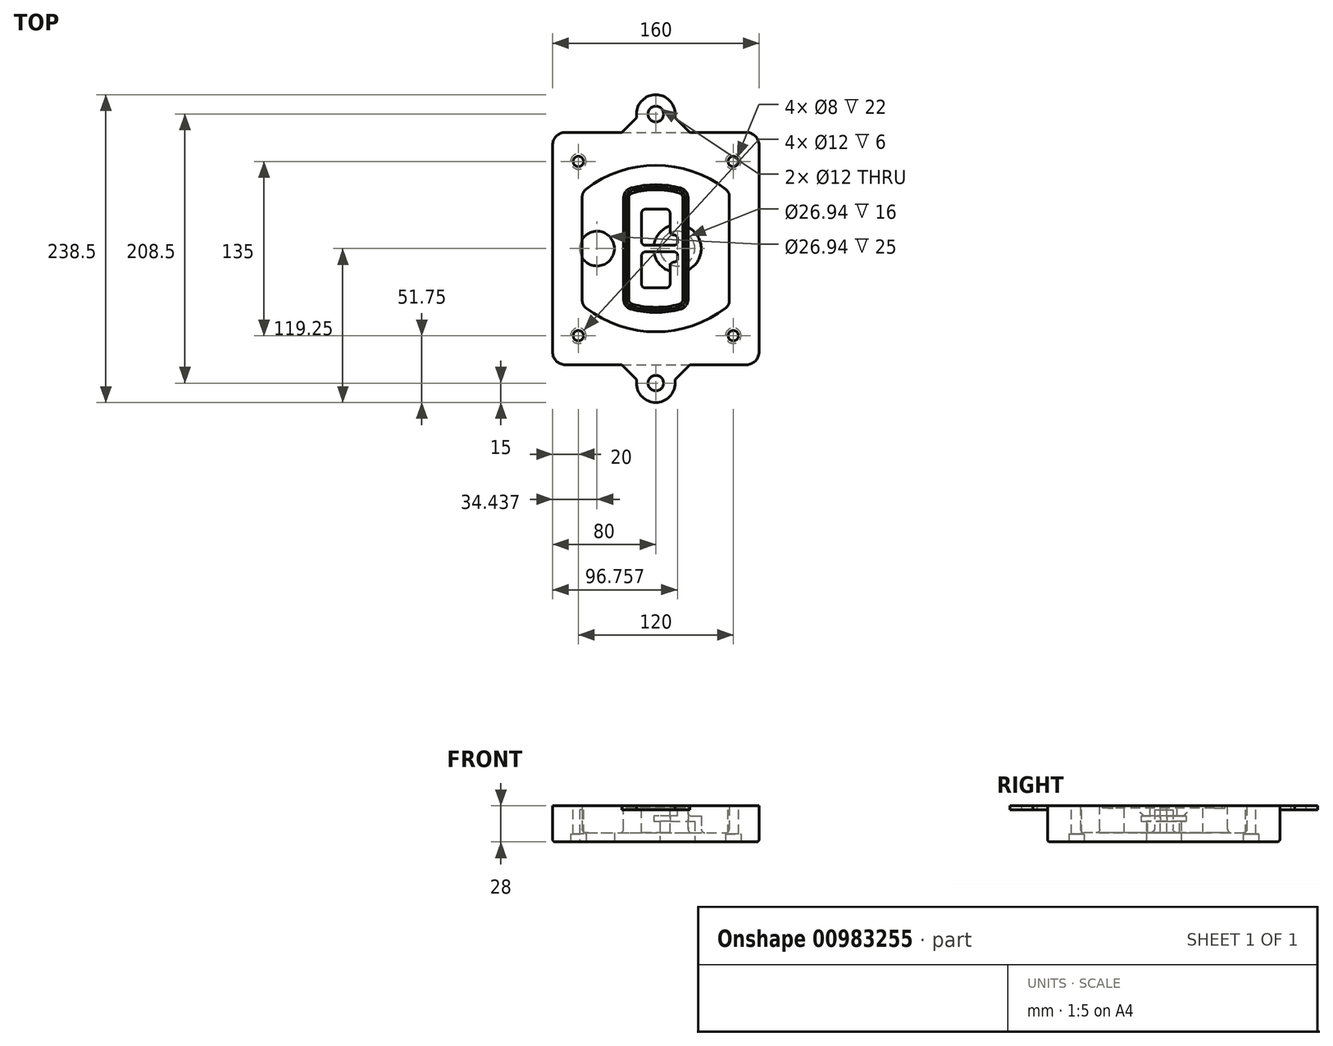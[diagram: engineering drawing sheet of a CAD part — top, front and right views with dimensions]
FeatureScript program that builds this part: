
annotation { "Feature Type Name" : "Feature", "Feature Type Description" : "" }
export const myFeature = defineFeature(function(context is Context, id is Id, definition is map)
    precondition{}
    {
        {
            var Q0;
            Q0=qCreatedBy(makeId("Top.planeOp"),FACE);
            var sketch = newSketch(context, id + "F0", { "sketchPlane" : qUnion([Q0])});
            skPoint(sketch, "E0.rect.middle", {"position": v(0, 0) * mm});
            skLineSegment(sketch, "E1.bottom", {"start": v(-70, -90) * mm, "end": v(70, -90) * mm});
            skLineSegment(sketch, "E1.top", {"start": v(-70, 90) * mm, "end": v(70, 90) * mm});
            skLineSegment(sketch, "E1.left", {"start": v(-80, -80) * mm, "end": v(-80, 80) * mm});
            skLineSegment(sketch, "E1.right", {"start": v(80, -80) * mm, "end": v(80, 80) * mm});
            skLineSegment(sketch, "E2", {"start": v(-80, 90) * mm, "end": v(80, -90) * mm, "construction": true});
            skLineSegment(sketch, "E3", {"start": v(80, 90) * mm, "end": v(-80, -90) * mm, "construction": true});
            skCircle(sketch, "E4", {"center": v(-60, 67.5) * mm, "radius": 4 * mm});
            skCircle(sketch, "E5", {"center": v(60, 67.5) * mm, "radius": 4 * mm});
            skCircle(sketch, "E6", {"center": v(60, -67.5) * mm, "radius": 4 * mm});
            skCircle(sketch, "E7", {"center": v(-60, -67.5) * mm, "radius": 4 * mm});
            skLineSegment(sketch, "E8", {"start": v(-60, 67.5) * mm, "end": v(60, 67.5) * mm, "construction": true});
            skLineSegment(sketch, "E9", {"start": v(60, 67.5) * mm, "end": v(60, -67.5) * mm, "construction": true});
            skLineSegment(sketch, "E10", {"start": v(60, -67.5) * mm, "end": v(-60, -67.5) * mm, "construction": true});
            skLineSegment(sketch, "E11", {"start": v(-60, -67.5) * mm, "end": v(-60, 67.5) * mm, "construction": true});
            skLineSegment(sketch, "E12", {"start": v(-60, 40.3) * mm, "end": v(-60, -40.3) * mm});
            skLineSegment(sketch, "E13", {"start": v(60, 40.3) * mm, "end": v(60, -40.3) * mm});
            skArc(sketch, "E14", {"start": v(56.15, 48.18) * mm, "mid": v(0, 67.5) * mm, "end": v(-56.15, 48.18) * mm});
            skArc(sketch, "E15", {"start": v(-56.15, -48.18) * mm, "mid": v(0, -67.5) * mm, "end": v(56.15, -48.18) * mm});
            skLineSegment(sketch, "E16", {"start": v(-60, 0) * mm, "end": v(60, 0) * mm, "construction": true});
            skPoint(sketch, "E17.visualSharp", {"position": v(-60, -45) * mm});
            skArc(sketch, "E17.filletArc", {"start": v(-60, -40.3) * mm, "mid": v(-58.99, -44.68) * mm, "end": v(-56.15, -48.18) * mm});
            skPoint(sketch, "E18.visualSharp", {"position": v(-60, 45) * mm});
            skArc(sketch, "E18.filletArc", {"start": v(-56.15, 48.18) * mm, "mid": v(-58.99, 44.68) * mm, "end": v(-60, 40.3) * mm});
            skPoint(sketch, "E19.visualSharp", {"position": v(60, 45) * mm});
            skArc(sketch, "E19.filletArc", {"start": v(60, 40.3) * mm, "mid": v(58.99, 44.68) * mm, "end": v(56.15, 48.18) * mm});
            skPoint(sketch, "E20.visualSharp", {"position": v(60, -45) * mm});
            skArc(sketch, "E20.filletArc", {"start": v(56.15, -48.18) * mm, "mid": v(58.99, -44.68) * mm, "end": v(60, -40.3) * mm});
            skPoint(sketch, "E21.visualSharp", {"position": v(-80, 90) * mm});
            skArc(sketch, "E21.filletArc", {"start": v(-70, 90) * mm, "mid": v(-77.07, 87.07) * mm, "end": v(-80, 80) * mm});
            skPoint(sketch, "E22.visualSharp", {"position": v(80, 90) * mm});
            skArc(sketch, "E22.filletArc", {"start": v(80, 80) * mm, "mid": v(77.07, 87.07) * mm, "end": v(70, 90) * mm});
            skPoint(sketch, "E23.visualSharp", {"position": v(80, -90) * mm});
            skArc(sketch, "E23.filletArc", {"start": v(70, -90) * mm, "mid": v(77.07, -87.07) * mm, "end": v(80, -80) * mm});
            skPoint(sketch, "E24.visualSharp", {"position": v(-80, -90) * mm});
            skArc(sketch, "E24.filletArc", {"start": v(-80, -80) * mm, "mid": v(-77.07, -87.07) * mm, "end": v(-70, -90) * mm});
            skArc(sketch, "E25.0", {"start": v(57, 40.3) * mm, "mid": v(56.3, 43.36) * mm, "end": v(54.3, 45.81) * mm});
            skLineSegment(sketch, "E25.1", {"start": v(57, 40.3) * mm, "end": v(57, -40.3) * mm});
            skArc(sketch, "E25.2", {"start": v(54.3, -45.81) * mm, "mid": v(56.3, -43.36) * mm, "end": v(57, -40.3) * mm});
            skArc(sketch, "E25.3", {"start": v(-54.3, -45.81) * mm, "mid": v(0, -64.5) * mm, "end": v(54.3, -45.81) * mm});
            skArc(sketch, "E25.4", {"start": v(-57, -40.3) * mm, "mid": v(-56.3, -43.36) * mm, "end": v(-54.3, -45.81) * mm});
            skArc(sketch, "E25.5", {"start": v(54.3, 45.81) * mm, "mid": v(0, 64.5) * mm, "end": v(-54.3, 45.81) * mm});
            skLineSegment(sketch, "E25.6", {"start": v(-57, 40.3) * mm, "end": v(-57, -40.3) * mm});
            skArc(sketch, "E25.7", {"start": v(-54.3, 45.81) * mm, "mid": v(-56.3, 43.36) * mm, "end": v(-57, 40.3) * mm});
            skArc(sketch, "E26.0", {"start": v(-58.62, 51.33) * mm, "mid": v(-62.58, 46.43) * mm, "end": v(-64, 40.3) * mm});
            skArc(sketch, "E26.1", {"start": v(58.62, 51.33) * mm, "mid": v(0, 71.5) * mm, "end": v(-58.62, 51.33) * mm});
            skArc(sketch, "E26.2", {"start": v(64, 40.3) * mm, "mid": v(62.58, 46.43) * mm, "end": v(58.62, 51.33) * mm});
            skLineSegment(sketch, "E26.3", {"start": v(64, 40.3) * mm, "end": v(64, -40.3) * mm});
            skArc(sketch, "E26.4", {"start": v(58.62, -51.33) * mm, "mid": v(62.58, -46.43) * mm, "end": v(64, -40.3) * mm});
            skLineSegment(sketch, "E26.5", {"start": v(-64, 40.3) * mm, "end": v(-64, -40.3) * mm});
            skArc(sketch, "E26.6", {"start": v(-58.62, -51.33) * mm, "mid": v(0, -71.5) * mm, "end": v(58.62, -51.33) * mm});
            skArc(sketch, "E26.7", {"start": v(-64, -40.3) * mm, "mid": v(-62.58, -46.43) * mm, "end": v(-58.62, -51.33) * mm});
            skSolve(sketch);
        }
        {
            var Q0;
            Q0=makeQuery(id+"F0.imprint","IMPRINT",FACE,{"disambiguationData":[TD([[makeQuery(id+"F0.imprint","IMPRINT",EDGE,{"derivedFrom":sQuery(id+"F0.wireOp",EDGE,"E1.bottom")}),1.0]])]});
            var Q1;
            Q1=makeQuery(id+"F0.imprint","IMPRINT",FACE,{"disambiguationData":[TD([[makeQuery(id+"F0.imprint","IMPRINT",EDGE,{"derivedFrom":sQuery(id+"F0.wireOp",EDGE,"E12")}),1.0]])]});
            var Q2;
            Q2=makeQuery(id+"F0.imprint","IMPRINT",FACE,{"disambiguationData":[TD([[makeQuery(id+"F0.imprint","IMPRINT",EDGE,{"derivedFrom":sQuery(id+"F0.wireOp",EDGE,"E25.0")}),1.0]])]});
            var Q3;
            Q3=makeQuery(id+"F0.imprint","IMPRINT",FACE,{"disambiguationData":[TD([[makeQuery(id+"F0.imprint","IMPRINT",EDGE,{"derivedFrom":sQuery(id+"F0.wireOp",EDGE,"E12")}),-1.0]])]});
            extrude(context, id + "F1", {"entities" : qUnion([Q0, Q1, Q2, Q3]), "oppositeDirection" : true, "depth" : 25 * mm});
        }
        {
            var Q0;
            Q0=makeQuery(id+"F0.imprint","IMPRINT",FACE,{"disambiguationData":[TD([[makeQuery(id+"F0.imprint","IMPRINT",EDGE,{"derivedFrom":sQuery(id+"F0.wireOp",EDGE,"E12")}),1.0]])]});
            extrude(context, id + "F2", {"entities" : qUnion([Q0]), "operationType" : NewBodyOperationType.ADD, "depth" : 3 * mm});
        }
        {
            var Q0;
            Q0=makeQuery(id+"F0.imprint","IMPRINT",FACE,{"disambiguationData":[TD([[makeQuery(id+"F0.imprint","IMPRINT",EDGE,{"derivedFrom":sQuery(id+"F0.wireOp",EDGE,"E25.0")}),1.0]])]});
            extrude(context, id + "F3", {"entities" : qUnion([Q0]), "operationType" : NewBodyOperationType.REMOVE, "oppositeDirection" : true, "depth" : 18 * mm});
        }
        {
            var Q0;
            Q0=makeQuery(id+"F2.opExtrude","CAP_FACE",FACE,{"disambiguationData":[OSD([sQuery(id+"F0.wireOp",EDGE,"E12"),sQuery(id+"F0.wireOp",EDGE,"E13"),sQuery(id+"F0.wireOp",EDGE,"E14"),sQuery(id+"F0.wireOp",EDGE,"E15"),sQuery(id+"F0.wireOp",EDGE,"E17.filletArc"),sQuery(id+"F0.wireOp",EDGE,"E18.filletArc"),sQuery(id+"F0.wireOp",EDGE,"E19.filletArc"),sQuery(id+"F0.wireOp",EDGE,"E20.filletArc"),sQuery(id+"F0.wireOp",EDGE,"E25.0"),sQuery(id+"F0.wireOp",EDGE,"E25.1"),sQuery(id+"F0.wireOp",EDGE,"E25.2"),sQuery(id+"F0.wireOp",EDGE,"E25.3"),sQuery(id+"F0.wireOp",EDGE,"E25.4"),sQuery(id+"F0.wireOp",EDGE,"E25.5"),sQuery(id+"F0.wireOp",EDGE,"E25.6"),sQuery(id+"F0.wireOp",EDGE,"E25.7")])],"isStart":false});
            var sketch = newSketch(context, id + "F4", { "sketchPlane" : qUnion([Q0])});
            skArc(sketch, "E27.0", {"start": v(-19.08, -46.97) * mm, "mid": v(0, -49.5) * mm, "end": v(19.08, -46.97) * mm});
            skArc(sketch, "E28.0", {"start": v(19.08, 46.97) * mm, "mid": v(0, 49.5) * mm, "end": v(-19.08, 46.97) * mm});
            skLineSegment(sketch, "E29", {"start": v(-25, 39.25) * mm, "end": v(-25, -39.25) * mm});
            skLineSegment(sketch, "E30", {"start": v(25, 39.25) * mm, "end": v(25, -39.25) * mm});
            skLineSegment(sketch, "E31", {"start": v(-25, 45.1) * mm, "end": v(25, 45.1) * mm, "construction": true});
            skLineSegment(sketch, "E32", {"start": v(-25, -45.1) * mm, "end": v(25, -45.1) * mm, "construction": true});
            skPoint(sketch, "E33.visualSharp", {"position": v(-25, 45.1) * mm});
            skArc(sketch, "E33.filletArc", {"start": v(-19.08, 46.97) * mm, "mid": v(-23.35, 44.11) * mm, "end": v(-25, 39.25) * mm});
            skPoint(sketch, "E34.visualSharp", {"position": v(25, 45.1) * mm});
            skArc(sketch, "E34.filletArc", {"start": v(25, 39.25) * mm, "mid": v(23.35, 44.11) * mm, "end": v(19.08, 46.97) * mm});
            skPoint(sketch, "E35.visualSharp", {"position": v(25, -45.1) * mm});
            skArc(sketch, "E35.filletArc", {"start": v(19.08, -46.97) * mm, "mid": v(23.35, -44.11) * mm, "end": v(25, -39.25) * mm});
            skPoint(sketch, "E36.visualSharp", {"position": v(-25, -45.1) * mm});
            skArc(sketch, "E36.filletArc", {"start": v(-25, -39.25) * mm, "mid": v(-23.35, -44.11) * mm, "end": v(-19.08, -46.97) * mm});
            skArc(sketch, "E37.0", {"start": v(54.3, 45.81) * mm, "mid": v(0, 64.5) * mm, "end": v(-54.3, 45.81) * mm});
            skArc(sketch, "E37.1", {"start": v(-54.3, 45.81) * mm, "mid": v(-56.3, 43.36) * mm, "end": v(-57, 40.3) * mm});
            skLineSegment(sketch, "E37.2", {"start": v(-57, 40.3) * mm, "end": v(-57, -40.3) * mm});
            skArc(sketch, "E37.3", {"start": v(-57, -40.3) * mm, "mid": v(-56.3, -43.36) * mm, "end": v(-54.3, -45.81) * mm});
            skArc(sketch, "E37.4", {"start": v(-54.3, -45.81) * mm, "mid": v(0, -64.5) * mm, "end": v(54.3, -45.81) * mm});
            skArc(sketch, "E37.5", {"start": v(54.3, -45.81) * mm, "mid": v(56.3, -43.36) * mm, "end": v(57, -40.3) * mm});
            skLineSegment(sketch, "E37.6", {"start": v(57, 40.3) * mm, "end": v(57, -40.3) * mm});
            skArc(sketch, "E37.7", {"start": v(57, 40.3) * mm, "mid": v(56.3, 43.36) * mm, "end": v(54.3, 45.81) * mm});
            skLineSegment(sketch, "E38.0", {"start": v(23, 39.25) * mm, "end": v(23, -39.25) * mm});
            skArc(sketch, "E38.1", {"start": v(18.56, -45.04) * mm, "mid": v(21.76, -42.9) * mm, "end": v(23, -39.25) * mm});
            skArc(sketch, "E38.2", {"start": v(-18.56, -45.04) * mm, "mid": v(0, -47.5) * mm, "end": v(18.56, -45.04) * mm});
            skArc(sketch, "E38.3", {"start": v(-23, -39.25) * mm, "mid": v(-21.76, -42.9) * mm, "end": v(-18.56, -45.04) * mm});
            skLineSegment(sketch, "E38.4", {"start": v(-23, 39.25) * mm, "end": v(-23, -39.25) * mm});
            skArc(sketch, "E38.5", {"start": v(23, 39.25) * mm, "mid": v(21.76, 42.9) * mm, "end": v(18.56, 45.04) * mm});
            skArc(sketch, "E38.6", {"start": v(-18.56, 45.04) * mm, "mid": v(-21.76, 42.9) * mm, "end": v(-23, 39.25) * mm});
            skArc(sketch, "E38.7", {"start": v(18.56, 45.04) * mm, "mid": v(0, 47.5) * mm, "end": v(-18.56, 45.04) * mm});
            skArc(sketch, "E39.0", {"start": v(21, 39.25) * mm, "mid": v(20.18, 41.68) * mm, "end": v(18.04, 43.1) * mm});
            skLineSegment(sketch, "E39.1", {"start": v(21, 39.25) * mm, "end": v(21, -39.25) * mm});
            skArc(sketch, "E39.2", {"start": v(18.04, -43.1) * mm, "mid": v(20.18, -41.68) * mm, "end": v(21, -39.25) * mm});
            skArc(sketch, "E39.3", {"start": v(-18.04, -43.1) * mm, "mid": v(0, -45.5) * mm, "end": v(18.04, -43.1) * mm});
            skArc(sketch, "E39.4", {"start": v(-21, -39.25) * mm, "mid": v(-20.18, -41.68) * mm, "end": v(-18.04, -43.1) * mm});
            skArc(sketch, "E39.5", {"start": v(18.04, 43.1) * mm, "mid": v(0, 45.5) * mm, "end": v(-18.04, 43.1) * mm});
            skLineSegment(sketch, "E39.6", {"start": v(-21, 39.25) * mm, "end": v(-21, -39.25) * mm});
            skArc(sketch, "E39.7", {"start": v(-18.04, 43.1) * mm, "mid": v(-20.18, 41.68) * mm, "end": v(-21, 39.25) * mm});
            skLineSegment(sketch, "E40", {"start": v(-25, 0) * mm, "end": v(25, 0) * mm, "construction": true});
            skLineSegment(sketch, "E41", {"start": v(-11, 5.5) * mm, "end": v(-11, 27.5) * mm});
            skLineSegment(sketch, "E42", {"start": v(-8, 30.5) * mm, "end": v(8, 30.5) * mm});
            skLineSegment(sketch, "E43", {"start": v(11, 27.5) * mm, "end": v(11, 13.5) * mm});
            skLineSegment(sketch, "E44", {"start": v(14, 10.5) * mm, "end": v(14, 10.5) * mm});
            skLineSegment(sketch, "E45", {"start": v(17, 7.5) * mm, "end": v(17, 5.5) * mm});
            skLineSegment(sketch, "E46", {"start": v(14, 2.5) * mm, "end": v(-8, 2.5) * mm});
            skPoint(sketch, "E47.visualSharp", {"position": v(-11, 30.5) * mm});
            skArc(sketch, "E47.filletArc", {"start": v(-8, 30.5) * mm, "mid": v(-10.12, 29.62) * mm, "end": v(-11, 27.5) * mm});
            skPoint(sketch, "E48.visualSharp", {"position": v(11, 30.5) * mm});
            skArc(sketch, "E48.filletArc", {"start": v(11, 27.5) * mm, "mid": v(10.12, 29.62) * mm, "end": v(8, 30.5) * mm});
            skPoint(sketch, "E49.visualSharp", {"position": v(11, 10.5) * mm});
            skArc(sketch, "E49.filletArc", {"start": v(11, 13.5) * mm, "mid": v(11.88, 11.38) * mm, "end": v(14, 10.5) * mm});
            skPoint(sketch, "E50.visualSharp", {"position": v(17, 10.5) * mm});
            skArc(sketch, "E50.filletArc", {"start": v(17, 7.5) * mm, "mid": v(16.12, 9.62) * mm, "end": v(14, 10.5) * mm});
            skPoint(sketch, "E51.visualSharp", {"position": v(17, 2.5) * mm});
            skArc(sketch, "E51.filletArc", {"start": v(14, 2.5) * mm, "mid": v(16.12, 3.38) * mm, "end": v(17, 5.5) * mm});
            skPoint(sketch, "E52.visualSharp", {"position": v(-11, 2.5) * mm});
            skArc(sketch, "E52.filletArc", {"start": v(-11, 5.5) * mm, "mid": v(-10.12, 3.38) * mm, "end": v(-8, 2.5) * mm});
            skLineSegment(sketch, "E53.0.MirrorCS", {"start": v(14, -2.5) * mm, "end": v(-8, -2.5) * mm});
            skArc(sketch, "E54.0.MirrorCS", {"start": v(-11, -5.5) * mm, "mid": v(-10.12, -3.38) * mm, "end": v(-8, -2.5) * mm});
            skLineSegment(sketch, "E55.0.MirrorCS", {"start": v(-11, -5.5) * mm, "end": v(-11, -27.5) * mm});
            skArc(sketch, "E56.0.MirrorCS", {"start": v(-8, -30.5) * mm, "mid": v(-10.12, -29.62) * mm, "end": v(-11, -27.5) * mm});
            skLineSegment(sketch, "E57.0.MirrorCS", {"start": v(-8, -30.5) * mm, "end": v(8, -30.5) * mm});
            skArc(sketch, "E58.0.MirrorCS", {"start": v(11, -27.5) * mm, "mid": v(10.12, -29.62) * mm, "end": v(8, -30.5) * mm});
            skLineSegment(sketch, "E59.0.MirrorCS", {"start": v(11, -27.5) * mm, "end": v(11, -13.5) * mm});
            skArc(sketch, "E60.0.MirrorCS", {"start": v(11, -13.5) * mm, "mid": v(11.88, -11.38) * mm, "end": v(14, -10.5) * mm});
            skArc(sketch, "E61.0.MirrorCS", {"start": v(17, -7.5) * mm, "mid": v(16.12, -9.62) * mm, "end": v(14, -10.5) * mm});
            skLineSegment(sketch, "E62.0.MirrorCS", {"start": v(17, -7.5) * mm, "end": v(17, -5.5) * mm});
            skArc(sketch, "E63.0.MirrorCS", {"start": v(14, -2.5) * mm, "mid": v(16.12, -3.38) * mm, "end": v(17, -5.5) * mm});
            skSolve(sketch);
        }
        {
            var Q0;
            Q0=makeQuery(id+"F4.imprint","IMPRINT",FACE,{"disambiguationData":[TD([[makeQuery(id+"F4.imprint","IMPRINT",EDGE,{"derivedFrom":sQuery(id+"F4.wireOp",EDGE,"E27.0")}),1.0]])]});
            var Q1;
            Q1=makeQuery(id+"F4.imprint","IMPRINT",FACE,{"disambiguationData":[TD([[makeQuery(id+"F4.imprint","IMPRINT",EDGE,{"derivedFrom":sQuery(id+"F4.wireOp",EDGE,"E38.0")}),-1.0]])]});
            var Q2;
            Q2=makeQuery(id+"F4.imprint","IMPRINT",FACE,{"disambiguationData":[TD([[makeQuery(id+"F4.imprint","IMPRINT",EDGE,{"derivedFrom":sQuery(id+"F4.wireOp",EDGE,"E39.0")}),1.0]])]});
            extrude(context, id + "F5", {"entities" : qUnion([Q0, Q1, Q2]), "operationType" : NewBodyOperationType.ADD, "endBound" : BoundingType.UP_TO_NEXT, "oppositeDirection" : true, "depth" : 25 * mm});
        }
        {
            var Q0;
            Q0=makeQuery(id+"F4.imprint","IMPRINT",FACE,{"disambiguationData":[TD([[makeQuery(id+"F4.imprint","IMPRINT",EDGE,{"derivedFrom":sQuery(id+"F4.wireOp",EDGE,"E38.0")}),-1.0]])]});
            extrude(context, id + "F6", {"entities" : qUnion([Q0]), "operationType" : NewBodyOperationType.REMOVE, "oppositeDirection" : true, "depth" : 2 * mm});
        }
        {
            var Q0;
            Q0=makeQuery(id+"F1.opExtrude","CAP_FACE",FACE,{"disambiguationData":[OSD([sQuery(id+"F0.wireOp",EDGE,"E1.bottom"),sQuery(id+"F0.wireOp",EDGE,"E1.top"),sQuery(id+"F0.wireOp",EDGE,"E1.left"),sQuery(id+"F0.wireOp",EDGE,"E1.right"),sQuery(id+"F0.wireOp",EDGE,"E4"),sQuery(id+"F0.wireOp",EDGE,"E5"),sQuery(id+"F0.wireOp",EDGE,"E6"),sQuery(id+"F0.wireOp",EDGE,"E7"),sQuery(id+"F0.wireOp",EDGE,"E21.filletArc"),sQuery(id+"F0.wireOp",EDGE,"E22.filletArc"),sQuery(id+"F0.wireOp",EDGE,"E23.filletArc"),sQuery(id+"F0.wireOp",EDGE,"E24.filletArc")])],"isStart":false});
            var sketch = newSketch(context, id + "F7", { "sketchPlane" : qUnion([Q0])});
            skCircle(sketch, "E64", {"center": v(16.76, 0) * mm, "radius": 13.47 * mm});
            skCircle(sketch, "E65", {"center": v(-45.56, 0) * mm, "radius": 13.47 * mm});
            skLineSegment(sketch, "E66", {"start": v(80, 0) * mm, "end": v(-80, 0) * mm});
            skCircle(sketch, "E67", {"center": v(16.76, 0) * mm, "radius": 18.47 * mm});
            skCircle(sketch, "E68", {"center": v(60, -67.5) * mm, "radius": 6 * mm});
            skCircle(sketch, "E69", {"center": v(-60, -67.5) * mm, "radius": 6 * mm});
            skCircle(sketch, "E70", {"center": v(-60, 67.5) * mm, "radius": 6 * mm});
            skCircle(sketch, "E71", {"center": v(60, 67.5) * mm, "radius": 6 * mm});
            skSolve(sketch);
        }
        {
            var Q0;
            {var subQ1=sQuery(id+"F7.wireOp",EDGE,"E66");var subQ4=sQuery(id+"F7.wireOp",EDGE,"E64");var subQ6=makeQuery(id+"F7.imprint","INTERSECT",VERTEX,{"disambiguationData":[OD(0.0)],"derivedFrom":[subQ4,subQ1]});Q0=makeQuery(id+"F7.imprint","IMPRINT",FACE,{"disambiguationData":[TD([[makeQuery(id+"F7.imprint","IMPRINT",EDGE,{"disambiguationData":[TD([[subQ6,-1.0]])],"derivedFrom":subQ4}),-1.0]])]});}
            var Q1;
            {var subQ0=sQuery(id+"F7.wireOp",EDGE,"E66");var subQ1=sQuery(id+"F7.wireOp",EDGE,"E64");var subQ3=makeQuery(id+"F7.imprint","INTERSECT",VERTEX,{"disambiguationData":[OD(0.0)],"derivedFrom":[subQ1,subQ0]});Q1=makeQuery(id+"F7.imprint","IMPRINT",FACE,{"disambiguationData":[TD([[makeQuery(id+"F7.imprint","IMPRINT",EDGE,{"disambiguationData":[TD([[subQ3,-1.0]])],"derivedFrom":subQ1}),1.0]])]});}
            var Q2;
            {var subQ0=sQuery(id+"F7.wireOp",EDGE,"E66");var subQ1=sQuery(id+"F7.wireOp",EDGE,"E64");var subQ3=makeQuery(id+"F7.imprint","INTERSECT",VERTEX,{"disambiguationData":[OD(0.0)],"derivedFrom":[subQ1,subQ0]});Q2=makeQuery(id+"F7.imprint","IMPRINT",FACE,{"disambiguationData":[TD([[makeQuery(id+"F7.imprint","IMPRINT",EDGE,{"disambiguationData":[TD([[subQ3,1.0]])],"derivedFrom":subQ1}),1.0]])]});}
            var Q3;
            {var subQ1=sQuery(id+"F7.wireOp",EDGE,"E66");var subQ4=sQuery(id+"F7.wireOp",EDGE,"E64");var subQ6=makeQuery(id+"F7.imprint","INTERSECT",VERTEX,{"disambiguationData":[OD(0.0)],"derivedFrom":[subQ4,subQ1]});Q3=makeQuery(id+"F7.imprint","IMPRINT",FACE,{"disambiguationData":[TD([[makeQuery(id+"F7.imprint","IMPRINT",EDGE,{"disambiguationData":[TD([[subQ6,1.0]])],"derivedFrom":subQ4}),-1.0]])]});}
            extrude(context, id + "F8", {"entities" : qUnion([Q0, Q1, Q2, Q3]), "operationType" : NewBodyOperationType.ADD, "oppositeDirection" : true, "depth" : 20 * mm});
        }
        {
            var Q0;
            {var subQ0=sQuery(id+"F7.wireOp",EDGE,"E66");var subQ1=sQuery(id+"F7.wireOp",EDGE,"E64");var subQ3=makeQuery(id+"F7.imprint","INTERSECT",VERTEX,{"disambiguationData":[OD(0.0)],"derivedFrom":[subQ1,subQ0]});Q0=makeQuery(id+"F7.imprint","IMPRINT",FACE,{"disambiguationData":[TD([[makeQuery(id+"F7.imprint","IMPRINT",EDGE,{"disambiguationData":[TD([[subQ3,-1.0]])],"derivedFrom":subQ1}),1.0]])]});}
            var Q1;
            {var subQ0=sQuery(id+"F7.wireOp",EDGE,"E66");var subQ1=sQuery(id+"F7.wireOp",EDGE,"E64");var subQ3=makeQuery(id+"F7.imprint","INTERSECT",VERTEX,{"disambiguationData":[OD(0.0)],"derivedFrom":[subQ1,subQ0]});Q1=makeQuery(id+"F7.imprint","IMPRINT",FACE,{"disambiguationData":[TD([[makeQuery(id+"F7.imprint","IMPRINT",EDGE,{"disambiguationData":[TD([[subQ3,1.0]])],"derivedFrom":subQ1}),1.0]])]});}
            extrude(context, id + "F9", {"entities" : qUnion([Q0, Q1]), "operationType" : NewBodyOperationType.REMOVE, "oppositeDirection" : true, "depth" : 16 * mm});
        }
        {
            var Q0;
            {var subQ0=sQuery(id+"F7.wireOp",EDGE,"E66");var subQ1=sQuery(id+"F7.wireOp",EDGE,"E65");var subQ3=makeQuery(id+"F7.imprint","INTERSECT",VERTEX,{"disambiguationData":[OD(0.0)],"derivedFrom":[subQ1,subQ0]});Q0=makeQuery(id+"F7.imprint","IMPRINT",FACE,{"disambiguationData":[TD([[makeQuery(id+"F7.imprint","IMPRINT",EDGE,{"disambiguationData":[TD([[subQ3,-1.0]])],"derivedFrom":subQ1}),1.0]])]});}
            var Q1;
            {var subQ0=sQuery(id+"F7.wireOp",EDGE,"E66");var subQ1=sQuery(id+"F7.wireOp",EDGE,"E65");var subQ3=makeQuery(id+"F7.imprint","INTERSECT",VERTEX,{"disambiguationData":[OD(0.0)],"derivedFrom":[subQ1,subQ0]});Q1=makeQuery(id+"F7.imprint","IMPRINT",FACE,{"disambiguationData":[TD([[makeQuery(id+"F7.imprint","IMPRINT",EDGE,{"disambiguationData":[TD([[subQ3,1.0]])],"derivedFrom":subQ1}),1.0]])]});}
            extrude(context, id + "F10", {"entities" : qUnion([Q0, Q1]), "operationType" : NewBodyOperationType.REMOVE, "oppositeDirection" : true, "depth" : 25 * mm});
        }
        {
            var Q0;
            Q0=makeQuery(id+"F7.imprint","IMPRINT",FACE,{"disambiguationData":[TD([[makeQuery(id+"F7.imprint","IMPRINT",EDGE,{"derivedFrom":sQuery(id+"F7.wireOp",EDGE,"E68")}),1.0]])]});
            var Q1;
            Q1=makeQuery(id+"F7.imprint","IMPRINT",FACE,{"disambiguationData":[TD([[makeQuery(id+"F7.imprint","IMPRINT",EDGE,{"derivedFrom":makeQuery(id+"F1.opExtrude","CAP_EDGE",EDGE,{"disambiguationData":[OSD([sQuery(id+"F0.wireOp",EDGE,"E5")])],"isStart":false})}),-1.0]])]});
            var Q2;
            Q2=makeQuery(id+"F7.imprint","IMPRINT",FACE,{"disambiguationData":[TD([[makeQuery(id+"F7.imprint","IMPRINT",EDGE,{"derivedFrom":sQuery(id+"F7.wireOp",EDGE,"E69")}),1.0]])]});
            var Q3;
            Q3=makeQuery(id+"F7.imprint","IMPRINT",FACE,{"disambiguationData":[TD([[makeQuery(id+"F7.imprint","IMPRINT",EDGE,{"derivedFrom":makeQuery(id+"F1.opExtrude","CAP_EDGE",EDGE,{"disambiguationData":[OSD([sQuery(id+"F0.wireOp",EDGE,"E4")])],"isStart":false})}),-1.0]])]});
            var Q4;
            Q4=makeQuery(id+"F7.imprint","IMPRINT",FACE,{"disambiguationData":[TD([[makeQuery(id+"F7.imprint","IMPRINT",EDGE,{"derivedFrom":sQuery(id+"F7.wireOp",EDGE,"E70")}),1.0]])]});
            var Q5;
            Q5=makeQuery(id+"F7.imprint","IMPRINT",FACE,{"disambiguationData":[TD([[makeQuery(id+"F7.imprint","IMPRINT",EDGE,{"derivedFrom":makeQuery(id+"F1.opExtrude","CAP_EDGE",EDGE,{"disambiguationData":[OSD([sQuery(id+"F0.wireOp",EDGE,"E7")])],"isStart":false})}),-1.0]])]});
            var Q6;
            Q6=makeQuery(id+"F7.imprint","IMPRINT",FACE,{"disambiguationData":[TD([[makeQuery(id+"F7.imprint","IMPRINT",EDGE,{"derivedFrom":sQuery(id+"F7.wireOp",EDGE,"E71")}),1.0]])]});
            var Q7;
            Q7=makeQuery(id+"F7.imprint","IMPRINT",FACE,{"disambiguationData":[TD([[makeQuery(id+"F7.imprint","IMPRINT",EDGE,{"derivedFrom":makeQuery(id+"F1.opExtrude","CAP_EDGE",EDGE,{"disambiguationData":[OSD([sQuery(id+"F0.wireOp",EDGE,"E6")])],"isStart":false})}),-1.0]])]});
            extrude(context, id + "F11", {"entities" : qUnion([Q0, Q1, Q2, Q3, Q4, Q5, Q6, Q7]), "operationType" : NewBodyOperationType.REMOVE, "oppositeDirection" : true, "depth" : 6 * mm});
        }
        {
            var Q0;
            Q0=makeQuery(id+"F9.boolean.opBoolean","COPY",FACE,{"derivedFrom":makeQuery(id+"F9.opExtrude","CAP_FACE",FACE,{"disambiguationData":[OSD([sQuery(id+"F7.wireOp",EDGE,"E64")])],"isStart":false})});
            var sketch = newSketch(context, id + "F12", { "sketchPlane" : qUnion([Q0])});
            skArc(sketch, "E72.0", {"start": v(11, 17.55) * mm, "mid": v(2.57, 11.82) * mm, "end": v(-1.54, 2.5) * mm});
            skArc(sketch, "E72.1", {"start": v(-1.54, -2.5) * mm, "mid": v(2.57, -11.82) * mm, "end": v(11, -17.55) * mm});
            skLineSegment(sketch, "E73", {"start": v(-1.54, -2.5) * mm, "end": v(14, -2.5) * mm});
            skLineSegment(sketch, "E74.0", {"start": v(14, 2.5) * mm, "end": v(-1.54, 2.5) * mm});
            skArc(sketch, "E74.1", {"start": v(14, 2.5) * mm, "mid": v(16.12, 3.38) * mm, "end": v(17, 5.5) * mm});
            skLineSegment(sketch, "E74.2", {"start": v(17, 7.5) * mm, "end": v(17, 5.5) * mm});
            skArc(sketch, "E74.3", {"start": v(17, 7.5) * mm, "mid": v(16.12, 9.62) * mm, "end": v(14, 10.5) * mm});
            skArc(sketch, "E74.4", {"start": v(11, 13.5) * mm, "mid": v(11.88, 11.38) * mm, "end": v(14, 10.5) * mm});
            skLineSegment(sketch, "E74.5", {"start": v(11, 17.55) * mm, "end": v(11, 13.5) * mm});
            skLineSegment(sketch, "E74.7", {"start": v(14, -2.5) * mm, "end": v(-1.54, -2.5) * mm});
            skArc(sketch, "E74.8", {"start": v(14, -2.5) * mm, "mid": v(16.12, -3.38) * mm, "end": v(17, -5.5) * mm});
            skLineSegment(sketch, "E74.9", {"start": v(17, -7.5) * mm, "end": v(17, -5.5) * mm});
            skArc(sketch, "E74.10", {"start": v(17, -7.5) * mm, "mid": v(16.12, -9.62) * mm, "end": v(14, -10.5) * mm});
            skArc(sketch, "E74.11", {"start": v(11, -13.5) * mm, "mid": v(11.88, -11.38) * mm, "end": v(14, -10.5) * mm});
            skLineSegment(sketch, "E74.12", {"start": v(11, -17.55) * mm, "end": v(11, -13.5) * mm});
            skPoint(sketch, "E75.orphan", {"position": v(11, -27.5) * mm});
            skPoint(sketch, "E76.orphan", {"position": v(-8, -2.5) * mm});
            skPoint(sketch, "E77.orphan", {"position": v(-8, 2.5) * mm});
            skPoint(sketch, "E78.orphan", {"position": v(11, 27.5) * mm});
            skSolve(sketch);
        }
        {
            var Q0;
            {var subQ7=sQuery(id+"F12.wireOp",EDGE,"E72.0");var subQ14=sQuery(id+"F12.wireOp",EDGE,"E72.1");var subQ16=sQuery(id+"F12.wireOp",EDGE,"E74.1");var subQ18=sQuery(id+"F12.wireOp",EDGE,"E74.8");Q0=qUnion([makeQuery(id+"F12.imprint","IMPRINT",FACE,{"disambiguationData":[TD([[makeQuery(id+"F12.imprint","IMPRINT",EDGE,{"derivedFrom":subQ7}),1.0]])]}),makeQuery(id+"F12.imprint","IMPRINT",FACE,{"disambiguationData":[TD([[makeQuery(id+"F12.imprint","IMPRINT",EDGE,{"derivedFrom":subQ14}),1.0]])]}),makeQuery(id+"F12.imprint","IMPRINT",FACE,{"disambiguationData":[TD([[makeQuery(id+"F12.imprint","IMPRINT",EDGE,{"derivedFrom":subQ16}),1.0]])]}),makeQuery(id+"F12.imprint","IMPRINT",FACE,{"disambiguationData":[TD([[makeQuery(id+"F12.imprint","IMPRINT",EDGE,{"derivedFrom":subQ18}),-1.0]])]})]);}
            var Q1;
            Q1=makeQuery(id+"F5.boolean.opBoolean","SPLIT",FACE,{"disambiguationData":[TD([makeQuery(id+"F5.opExtrude","SWEPT_FACE",FACE,{"disambiguationData":[OSD([sQuery(id+"F4.wireOp",EDGE,"E41")])]})])],"derivedFrom":makeQuery(id+"F3.boolean.opBoolean","COPY",FACE,{"derivedFrom":makeQuery(id+"F3.opExtrude","CAP_FACE",FACE,{"disambiguationData":[OSD([sQuery(id+"F0.wireOp",EDGE,"E25.0"),sQuery(id+"F0.wireOp",EDGE,"E25.1"),sQuery(id+"F0.wireOp",EDGE,"E25.2"),sQuery(id+"F0.wireOp",EDGE,"E25.3"),sQuery(id+"F0.wireOp",EDGE,"E25.4"),sQuery(id+"F0.wireOp",EDGE,"E25.5"),sQuery(id+"F0.wireOp",EDGE,"E25.6"),sQuery(id+"F0.wireOp",EDGE,"E25.7")])],"isStart":false})})});
            extrude(context, id + "F13", {"entities" : qUnion([Q0]), "operationType" : NewBodyOperationType.REMOVE, "endBound" : BoundingType.UP_TO_SURFACE, "endBoundEntityFace" : qUnion([Q1]), "depth" : 25 * mm});
        }
        {
            var Q0;
            Q0=makeQuery(id+"F3.boolean.opBoolean","COPY",EDGE,{"derivedFrom":makeQuery(id+"F3.opExtrude","CAP_EDGE",EDGE,{"disambiguationData":[OSD([sQuery(id+"F0.wireOp",EDGE,"E25.6")])],"isStart":false})});
            var Q1;
            Q1=makeQuery(id+"F8.boolean.opBoolean","INTERSECT",EDGE,{"derivedFrom":[makeQuery(id+"F5.opExtrude","SWEPT_FACE",FACE,{"disambiguationData":[OSD([sQuery(id+"F4.wireOp",EDGE,"E30")])]}),makeQuery(id+"F8.opExtrude","CAP_FACE",FACE,{"disambiguationData":[OSD([sQuery(id+"F7.wireOp",EDGE,"E67")])],"isStart":false})]});
            var Q2;
            Q2=makeQuery(id+"F8.boolean.opBoolean","INTERSECT",EDGE,{"disambiguationData":[OD(1.0)],"derivedFrom":[makeQuery(id+"F5.opExtrude","SWEPT_FACE",FACE,{"disambiguationData":[OSD([sQuery(id+"F4.wireOp",EDGE,"E30")])]}),makeQuery(id+"F8.opExtrude","SWEPT_FACE",FACE,{"disambiguationData":[OSD([sQuery(id+"F7.wireOp",EDGE,"E67")])]})]});
            var Q3;
            {var subQ0=sQuery(id+"F4.wireOp",EDGE,"E30");Q3=makeQuery(id+"F8.boolean.opBoolean","SPLIT",EDGE,{"disambiguationData":[TD([makeQuery(id+"F5.opExtrude","SWEPT_FACE",FACE,{"disambiguationData":[OSD([sQuery(id+"F4.wireOp",EDGE,"E35.filletArc")])]})])],"derivedFrom":makeQuery(id+"F5.opExtrude","CAP_EDGE",EDGE,{"disambiguationData":[OSD([subQ0])],"isStart":false})});}
            var Q4;
            {var subQ0=sQuery(id+"F0.wireOp",EDGE,"E25.7");var subQ1=sQuery(id+"F0.wireOp",EDGE,"E25.1");var subQ2=sQuery(id+"F0.wireOp",EDGE,"E25.6");var subQ3=sQuery(id+"F0.wireOp",EDGE,"E25.5");var subQ4=sQuery(id+"F0.wireOp",EDGE,"E25.4");var subQ5=sQuery(id+"F0.wireOp",EDGE,"E25.0");var subQ6=sQuery(id+"F0.wireOp",EDGE,"E25.2");var subQ7=sQuery(id+"F0.wireOp",EDGE,"E25.3");Q4=makeQuery(id+"F8.boolean.opBoolean","INTERSECT",EDGE,{"derivedFrom":[makeQuery(id+"F5.boolean.opBoolean","SPLIT",FACE,{"disambiguationData":[TD([makeQuery(id+"F2.opExtrude","SWEPT_FACE",FACE,{"disambiguationData":[OSD([subQ5])]})])],"derivedFrom":makeQuery(id+"F3.boolean.opBoolean","COPY",FACE,{"derivedFrom":makeQuery(id+"F3.opExtrude","CAP_FACE",FACE,{"disambiguationData":[OSD([subQ5,subQ1,subQ6,subQ7,subQ4,subQ3,subQ2,subQ0])],"isStart":false})})}),makeQuery(id+"F8.opExtrude","SWEPT_FACE",FACE,{"disambiguationData":[OSD([sQuery(id+"F7.wireOp",EDGE,"E67")])]})]});}
            var Q5;
            Q5=makeQuery(id+"F8.boolean.opBoolean","INTERSECT",EDGE,{"disambiguationData":[OD(0.0)],"derivedFrom":[makeQuery(id+"F5.opExtrude","SWEPT_FACE",FACE,{"disambiguationData":[OSD([sQuery(id+"F4.wireOp",EDGE,"E30")])]}),makeQuery(id+"F8.opExtrude","SWEPT_FACE",FACE,{"disambiguationData":[OSD([sQuery(id+"F7.wireOp",EDGE,"E67")])]})]});
            fillet(context, id + "F14", {"entities" : qUnion([Q0, Q1, Q2, Q3, Q4, Q5]), "radius" : 3 * mm, "tangentPropagation" : true, "allowEdgeOverflow" : false});
        }
        {
            var Q0;
            Q0=makeQuery(id+"F1.opExtrude","CAP_EDGE",EDGE,{"disambiguationData":[OSD([sQuery(id+"F0.wireOp",EDGE,"E1.bottom")])],"isStart":false});
            fillet(context, id + "F15", {"entities" : qUnion([Q0]), "radius" : 2 * mm, "tangentPropagation" : true, "allowEdgeOverflow" : false});
        }
        {
            var Q0;
            {var subQ0=sQuery(id+"F0.wireOp",EDGE,"E21.filletArc");var subQ1=sQuery(id+"F0.wireOp",EDGE,"E7");var subQ2=sQuery(id+"F0.wireOp",EDGE,"E6");var subQ3=sQuery(id+"F0.wireOp",EDGE,"E5");var subQ4=sQuery(id+"F0.wireOp",EDGE,"E4");var subQ5=sQuery(id+"F0.wireOp",EDGE,"E22.filletArc");var subQ6=sQuery(id+"F0.wireOp",EDGE,"E1.bottom");var subQ7=sQuery(id+"F0.wireOp",EDGE,"E1.right");var subQ8=sQuery(id+"F0.wireOp",EDGE,"E1.top");var subQ9=sQuery(id+"F0.wireOp",EDGE,"E1.left");var subQ10=sQuery(id+"F0.wireOp",EDGE,"E23.filletArc");var subQ11=sQuery(id+"F0.wireOp",EDGE,"E24.filletArc");Q0=makeQuery(id+"F2.boolean.opBoolean","SPLIT",FACE,{"disambiguationData":[TD([makeQuery(id+"F1.opExtrude","SWEPT_FACE",FACE,{"disambiguationData":[OSD([subQ6])]})])],"derivedFrom":makeQuery(id+"F1.opExtrude","CAP_FACE",FACE,{"disambiguationData":[OSD([subQ6,subQ8,subQ9,subQ7,subQ4,subQ3,subQ2,subQ1,subQ0,subQ5,subQ10,subQ11])],"isStart":true})});}
            var sketch = newSketch(context, id + "F16", { "sketchPlane" : qUnion([Q0])});
            skLineSegment(sketch, "E79", {"start": v(0, 90) * mm, "end": v(0, 104.25) * mm, "construction": true});
            skCircle(sketch, "E80", {"center": v(0, 104.25) * mm, "radius": 6 * mm});
            skArc(sketch, "E81", {"start": v(15, 104.25) * mm, "mid": v(0, 119.25) * mm, "end": v(-15, 104.25) * mm});
            skLineSegment(sketch, "E82", {"start": v(-15, 104.25) * mm, "end": v(-15, 101.47) * mm});
            skLineSegment(sketch, "E83", {"start": v(-15, 101.47) * mm, "end": v(-26.47, 90) * mm});
            skLineSegment(sketch, "E84.MirrorCS", {"start": v(15, 101.47) * mm, "end": v(26.47, 90) * mm});
            skLineSegment(sketch, "E85.MirrorCS", {"start": v(15, 104.25) * mm, "end": v(15, 101.47) * mm});
            skLineSegment(sketch, "E86", {"start": v(-80, 0) * mm, "end": v(80, 0) * mm, "construction": true});
            skArc(sketch, "E87.MirrorCS", {"start": v(-15, 104.25) * mm, "mid": v(0, 119.25) * mm, "end": v(15, 104.25) * mm});
            skLineSegment(sketch, "E88.MirrorCS", {"start": v(80, 0) * mm, "end": v(-80, 0) * mm, "construction": true});
            skLineSegment(sketch, "E89.MirrorCS", {"start": v(-15, -104.25) * mm, "end": v(-15, -101.47) * mm});
            skLineSegment(sketch, "E90.MirrorCS", {"start": v(15, -104.25) * mm, "end": v(15, -101.47) * mm});
            skCircle(sketch, "E91.MirrorC", {"center": v(0, -104.25) * mm, "radius": 6 * mm});
            skArc(sketch, "E92.MirrorCS", {"start": v(15, -104.25) * mm, "mid": v(0, -119.25) * mm, "end": v(-15, -104.25) * mm});
            skLineSegment(sketch, "E93.MirrorCS", {"start": v(15, -101.47) * mm, "end": v(26.47, -90) * mm});
            skLineSegment(sketch, "E94.MirrorCS", {"start": v(-15, -101.47) * mm, "end": v(-26.47, -90) * mm});
            skArc(sketch, "E95.MirrorCS", {"start": v(-15, -104.25) * mm, "mid": v(0, -119.25) * mm, "end": v(15, -104.25) * mm});
            skLineSegment(sketch, "E96.MirrorCS", {"start": v(0, -90) * mm, "end": v(0, -104.25) * mm, "construction": true});
            skLineSegment(sketch, "E97", {"start": v(-26.47, 90) * mm, "end": v(26.47, 90) * mm});
            skSolve(sketch);
        }
        {
            var Q0;
            Q0=makeQuery(id+"F16.imprint","IMPRINT",FACE,{"disambiguationData":[TD([[makeQuery(id+"F16.imprint","IMPRINT",EDGE,{"derivedFrom":sQuery(id+"F16.wireOp",EDGE,"E82")}),1.0]])]});
            var Q1;
            Q1=makeQuery(id+"F16.imprint","IMPRINT",FACE,{"disambiguationData":[TD([[makeQuery(id+"F16.imprint","IMPRINT",EDGE,{"derivedFrom":makeQuery(id+"F1.opExtrude","CAP_EDGE",EDGE,{"disambiguationData":[OSD([sQuery(id+"F0.wireOp",EDGE,"E1.left")])],"isStart":true})}),-1.0]])]});
            var Q2;
            Q2=makeQuery(id+"F16.imprint","IMPRINT",FACE,{"disambiguationData":[TD([[makeQuery(id+"F16.imprint","IMPRINT",EDGE,{"derivedFrom":sQuery(id+"F16.wireOp",EDGE,"E89.MirrorCS")}),-1.0]])]});
            var Q3;
            Q3=makeQuery(id+"F2.opExtrude","CAP_FACE",FACE,{"disambiguationData":[OSD([sQuery(id+"F0.wireOp",EDGE,"E12"),sQuery(id+"F0.wireOp",EDGE,"E13"),sQuery(id+"F0.wireOp",EDGE,"E14"),sQuery(id+"F0.wireOp",EDGE,"E15"),sQuery(id+"F0.wireOp",EDGE,"E17.filletArc"),sQuery(id+"F0.wireOp",EDGE,"E18.filletArc"),sQuery(id+"F0.wireOp",EDGE,"E19.filletArc"),sQuery(id+"F0.wireOp",EDGE,"E20.filletArc"),sQuery(id+"F0.wireOp",EDGE,"E25.0"),sQuery(id+"F0.wireOp",EDGE,"E25.1"),sQuery(id+"F0.wireOp",EDGE,"E25.2"),sQuery(id+"F0.wireOp",EDGE,"E25.3"),sQuery(id+"F0.wireOp",EDGE,"E25.4"),sQuery(id+"F0.wireOp",EDGE,"E25.5"),sQuery(id+"F0.wireOp",EDGE,"E25.6"),sQuery(id+"F0.wireOp",EDGE,"E25.7")])],"isStart":false});
            extrude(context, id + "F17", {"entities" : qUnion([Q0, Q1, Q2]), "operationType" : NewBodyOperationType.ADD, "endBound" : BoundingType.UP_TO_SURFACE, "depth" : 25 * mm, "endBoundEntityFace" : qUnion([Q3]), "offsetDistance" : 25 * mm});
        }
    });
